# Revit family: Haworth_Masters_Combo_Lateral
name_source: partatom
category: Furniture Systems
revit_build: Autodesk Revit 2018 (Build: 20170223_1515(x64)
units: mm (PartAtom-declared; Revit-internal decimal feet)

## family parameters
Always vertical = Yes
Cut with Voids When Loaded = No
OmniClass Number = 23.40.70.14.64.21
OmniClass Title = Systems Furniture
Part Type = Normal
Room Calculation Point = No
Round Connector Dimension = Use Diameter
Shared = No
Work Plane-Based = No

## types (2) — shared parameters
Actual Width = 35 7/8"
Assembly Code = E2020200
Bar Pull = No
Cabinet Finish = Haworth _ Wood _ White Oak
Classic Pull = Yes
Custom Size = No
Description = Haworth - Masters - Combo Lateral
Door Bar Pool Length = 8"
Door Pull Centerline = 13"
Door Width = 17 7/8"
Drawer Bar Pull Length = 29 1/2"
Drawer Height = 13"
Finger Pull = No
Front Finish = Haworth _ Wood _ White Oak
Hardware Finish = Haworth _ Metal _ Brushed Aluminum
Lateral File Height = 28"
Linear Pull = No
Manufacturer = Haworth
Max. Depth = 24"
Max. Width = 47 7/8"
Min. Depth = 19"
Min. Width = 29 7/8"
Model = Haworth - Masters - Combo Lateral
Revision Number = 3
Size = Verify Final Dim. w/ Haworth
Standard Depths = 19, 24 in.
Standard Widths = 30, 36 in.
Sustainability Info = http://www.haworth.com
URL = www.haworth.com
URL - Product = http://www.haworth.com
Warranty = http://www.haworth.com
Width = 36"

## per-type parameters (varying)
| type | Actual Depth | Actual Height | Depth | Door Height | Five High | Six High |
| Five High | 19" | 69" | 19" | 40 7/8" | Yes | No |
| Six High | 24" | 81 5/8" | 24" | 53 1/2" | No | Yes |

## geometry (parser evidence)
native form markers: Sweep x12
no freeform markers — native parametric forms only
